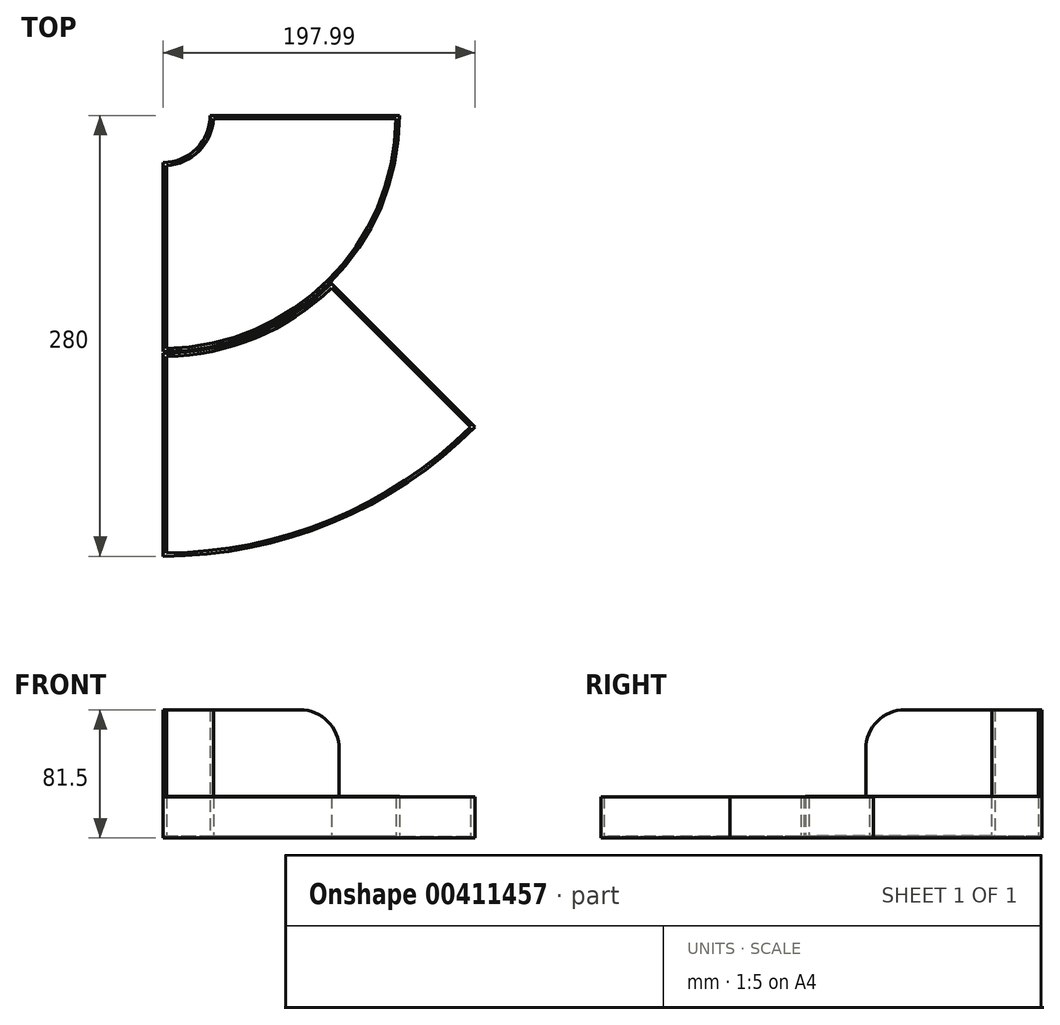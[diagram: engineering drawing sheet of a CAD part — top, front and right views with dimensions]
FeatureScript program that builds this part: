
annotation { "Feature Type Name" : "Feature", "Feature Type Description" : "" }
export const myFeature = defineFeature(function(context is Context, id is Id, definition is map)
    precondition{}
    {
        {
            var Q0;
            Q0=qCreatedBy(makeId("Top.planeOp"),FACE);
            var sketch = newSketch(context, id + "F0", { "sketchPlane" : qUnion([Q0])});
            skArc(sketch, "E0", {"start": v(0, 170) * mm, "mid": v(21.21, 178.79) * mm, "end": v(30, 200) * mm});
            skArc(sketch, "E1", {"start": v(0, 50) * mm, "mid": v(106.07, 93.93) * mm, "end": v(150, 200) * mm});
            skLineSegment(sketch, "E2", {"start": v(0, 170) * mm, "end": v(0, 50) * mm});
            skLineSegment(sketch, "E3", {"start": v(30, 200) * mm, "end": v(150, 200) * mm});
            skLineSegment(sketch, "E4", {"start": v(0, 200) * mm, "end": v(184.05, 200) * mm});
            skSolve(sketch);
        }
        {
            var Q0;
            Q0=makeQuery(id+"F0.imprint","IMPRINT",FACE,{"disambiguationData":[TD([[makeQuery(id+"F0.imprint","IMPRINT",EDGE,{"derivedFrom":sQuery(id+"F0.wireOp",EDGE,"E0")}),-1.0]])]});
            extrude(context, id + "F1", {"entities" : qUnion([Q0]), "depth" : 1.5 * mm, "offsetDistance" : 25 * mm});
        }
        {
            var Q0;
            Q0=makeQuery(id+"F1.opExtrude","CAP_FACE",FACE,{"disambiguationData":[OSD([sQuery(id+"F0.wireOp",EDGE,"E0"),sQuery(id+"F0.wireOp",EDGE,"E1"),sQuery(id+"F0.wireOp",EDGE,"E2"),sQuery(id+"F0.wireOp",EDGE,"E3")])],"isStart":false});
            var sketch = newSketch(context, id + "F2", { "sketchPlane" : qUnion([Q0])});
            skLineSegment(sketch, "E5", {"start": v(0, 170) * mm, "end": v(0, 170) * mm});
            skArc(sketch, "E6", {"start": v(0, 170) * mm, "mid": v(21.21, 178.79) * mm, "end": v(30, 200) * mm});
            skArc(sketch, "E7", {"start": v(0, 168) * mm, "mid": v(22.63, 177.37) * mm, "end": v(32, 200) * mm});
            skArc(sketch, "E8", {"start": v(0, 50) * mm, "mid": v(106.07, 93.93) * mm, "end": v(150, 200) * mm});
            skArc(sketch, "E9", {"start": v(0, 52) * mm, "mid": v(104.65, 95.35) * mm, "end": v(148, 200) * mm});
            skLineSegment(sketch, "E10", {"start": v(0, 170) * mm, "end": v(0, 50) * mm});
            skLineSegment(sketch, "E11", {"start": v(2, 168.06) * mm, "end": v(2, 52.01) * mm});
            skLineSegment(sketch, "E12", {"start": v(30, 200) * mm, "end": v(150, 200) * mm});
            skLineSegment(sketch, "E13", {"start": v(31.94, 198) * mm, "end": v(147.99, 198) * mm});
            skSolve(sketch);
        }
        {
            var Q0;
            Q0 = qSketchRegion(id + "F2", true);
            extrude(context, id + "F3", {"entities" : qUnion([Q0]), "operationType" : NewBodyOperationType.ADD, "depth" : 25 * mm, "offsetDistance" : 25 * mm});
        }
        {
            var Q0;
            Q0=qCreatedBy(makeId("Top.planeOp"),FACE);
            var sketch = newSketch(context, id + "F4", { "sketchPlane" : qUnion([Q0])});
            skArc(sketch, "E14", {"start": v(0, 49) * mm, "mid": v(57.79, 60.5) * mm, "end": v(106.77, 93.23) * mm});
            skArc(sketch, "E15", {"start": v(0, -80) * mm, "mid": v(107.15, -58.69) * mm, "end": v(197.99, 2.01) * mm});
            skLineSegment(sketch, "E16", {"start": v(0, 49) * mm, "end": v(0, -80) * mm});
            skLineSegment(sketch, "E17", {"start": v(106.77, 93.23) * mm, "end": v(197.99, 2.01) * mm});
            skSolve(sketch);
        }
        {
            var Q0;
            Q0 = qSketchRegion(id + "F4", true);
            extrude(context, id + "F5", {"entities" : qUnion([Q0]), "depth" : 1.2 * mm, "offsetDistance" : 25 * mm});
        }
        {
            var Q0;
            Q0=makeQuery(id+"F5.opExtrude","CAP_FACE",FACE,{"disambiguationData":[OSD([sQuery(id+"F4.wireOp",EDGE,"E14"),sQuery(id+"F4.wireOp",EDGE,"E15"),sQuery(id+"F4.wireOp",EDGE,"E16"),sQuery(id+"F4.wireOp",EDGE,"E17")])],"isStart":false});
            var sketch = newSketch(context, id + "F6", { "sketchPlane" : qUnion([Q0])});
            skArc(sketch, "E18", {"start": v(0, 49) * mm, "mid": v(57.79, 60.5) * mm, "end": v(106.77, 93.23) * mm});
            skArc(sketch, "E19", {"start": v(0, -80) * mm, "mid": v(107.15, -58.69) * mm, "end": v(197.99, 2.01) * mm});
            skArc(sketch, "E20", {"start": v(0, 47) * mm, "mid": v(58.55, 58.65) * mm, "end": v(108.19, 91.81) * mm});
            skArc(sketch, "E21", {"start": v(0, -78) * mm, "mid": v(106.39, -56.84) * mm, "end": v(196.58, 3.42) * mm});
            skLineSegment(sketch, "E22", {"start": v(106.77, 93.23) * mm, "end": v(197.99, 2.01) * mm});
            skLineSegment(sketch, "E23", {"start": v(0, 49) * mm, "end": v(0, -80) * mm});
            skLineSegment(sketch, "E24", {"start": v(2, 47.01) * mm, "end": v(2, -78) * mm});
            skLineSegment(sketch, "E25", {"start": v(106.76, 90.4) * mm, "end": v(195.16, 2.02) * mm});
            skSolve(sketch);
        }
        {
            var Q0;
            Q0 = qSketchRegion(id + "F6", true);
            extrude(context, id + "F7", {"entities" : qUnion([Q0]), "operationType" : NewBodyOperationType.ADD, "depth" : 25 * mm, "offsetDistance" : 25 * mm});
        }
        {
            var Q0;
            Q0=makeQuery(id+"F1.opExtrude","CAP_FACE",FACE,{"disambiguationData":[OSD([sQuery(id+"F0.wireOp",EDGE,"E0"),sQuery(id+"F0.wireOp",EDGE,"E1"),sQuery(id+"F0.wireOp",EDGE,"E2"),sQuery(id+"F0.wireOp",EDGE,"E3")])],"isStart":false});
            var sketch = newSketch(context, id + "F8", { "sketchPlane" : qUnion([Q0])});
            skArc(sketch, "E26", {"start": v(0, 170.12) * mm, "mid": v(21.13, 178.87) * mm, "end": v(29.88, 200) * mm});
            skArc(sketch, "E27", {"start": v(0, 168.12) * mm, "mid": v(22.54, 177.46) * mm, "end": v(31.88, 200) * mm});
            skLineSegment(sketch, "E28", {"start": v(0, 170.12) * mm, "end": v(0, 88.18) * mm});
            skLineSegment(sketch, "E29", {"start": v(2, 168.18) * mm, "end": v(2, 88.18) * mm});
            skLineSegment(sketch, "E30", {"start": v(29.88, 200) * mm, "end": v(111.82, 200) * mm});
            skLineSegment(sketch, "E31", {"start": v(31.82, 198) * mm, "end": v(111.82, 198) * mm});
            skLineSegment(sketch, "E32", {"start": v(0, 88.18) * mm, "end": v(2, 88.18) * mm});
            skLineSegment(sketch, "E33", {"start": v(111.82, 200) * mm, "end": v(111.82, 198) * mm});
            skSolve(sketch);
        }
        {
            var Q0;
            Q0 = qSketchRegion(id + "F8", true);
            extrude(context, id + "F9", {"entities" : qUnion([Q0]), "operationType" : NewBodyOperationType.ADD, "depth" : 80 * mm, "offsetDistance" : 25 * mm});
        }
        {
            var Q0;
            Q0=makeQuery(id+"F9.opExtrude","CAP_EDGE",EDGE,{"disambiguationData":[OSD([sQuery(id+"F8.wireOp",EDGE,"E33")])],"isStart":false});
            var Q1;
            Q1=makeQuery(id+"F9.opExtrude","CAP_EDGE",EDGE,{"disambiguationData":[OSD([sQuery(id+"F8.wireOp",EDGE,"E32")])],"isStart":false});
            fillet(context, id + "F10", {"entities" : qUnion([Q0, Q1]), "radius" : 25 * mm, "tangentPropagation" : true, "allowEdgeOverflow" : false});
        }
    });
